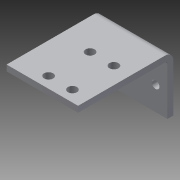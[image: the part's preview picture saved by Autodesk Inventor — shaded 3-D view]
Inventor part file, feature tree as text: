
AUTODESK INVENTOR PART (.ipt)
format: ipt  version: 2014 (Build 180170000, 170)  size: 129,536 bytes
history: native  units: in
note: dims shown in document units (in); Inventor stores cm internally (conversion verified against a paired STEP export)
features: sheet_metal_op x4, sketch x3, other x3
ambient origin geometry x8: Origin, YZ Plane, XZ Plane, XY Plane, X Axis, Y Axis, Z Axis, Center Point
bodies: Solid1 (feature_tree)
feature tree (10):
  sheet_metal_op  "Face1"
  sheet_metal_op  "Flange1"
  sketch  "Sketch1"  dims[d0=1.5in]
  other  "Plate1"
  sketch  "Sketch2"  dims[d1=1.0in]
  other  "Plate2"
  sheet_metal_op  "Bend1"
  sheet_metal_op  "Corner1"
  sketch  "Sketch3"  dims[d2=0.163in d3=0.5in d4=0.25in d5=0.7874in d7=1.0in d8=0.3937in d10=1.0in d12=0.125in d13=0.125in d14=0.0625in d15=0.25in d16=0.125in d17=2.0in d18=90.0deg d19=0.05in d20=0.5in d21=0.125in d22=0.125in d23=0.75in d24=1.31in d25=0.22in d26=0.125in d27=0.19in d29=0.5in d30=0.125in d31=0.0in d32=0.522in]
  other  "Cut1"
